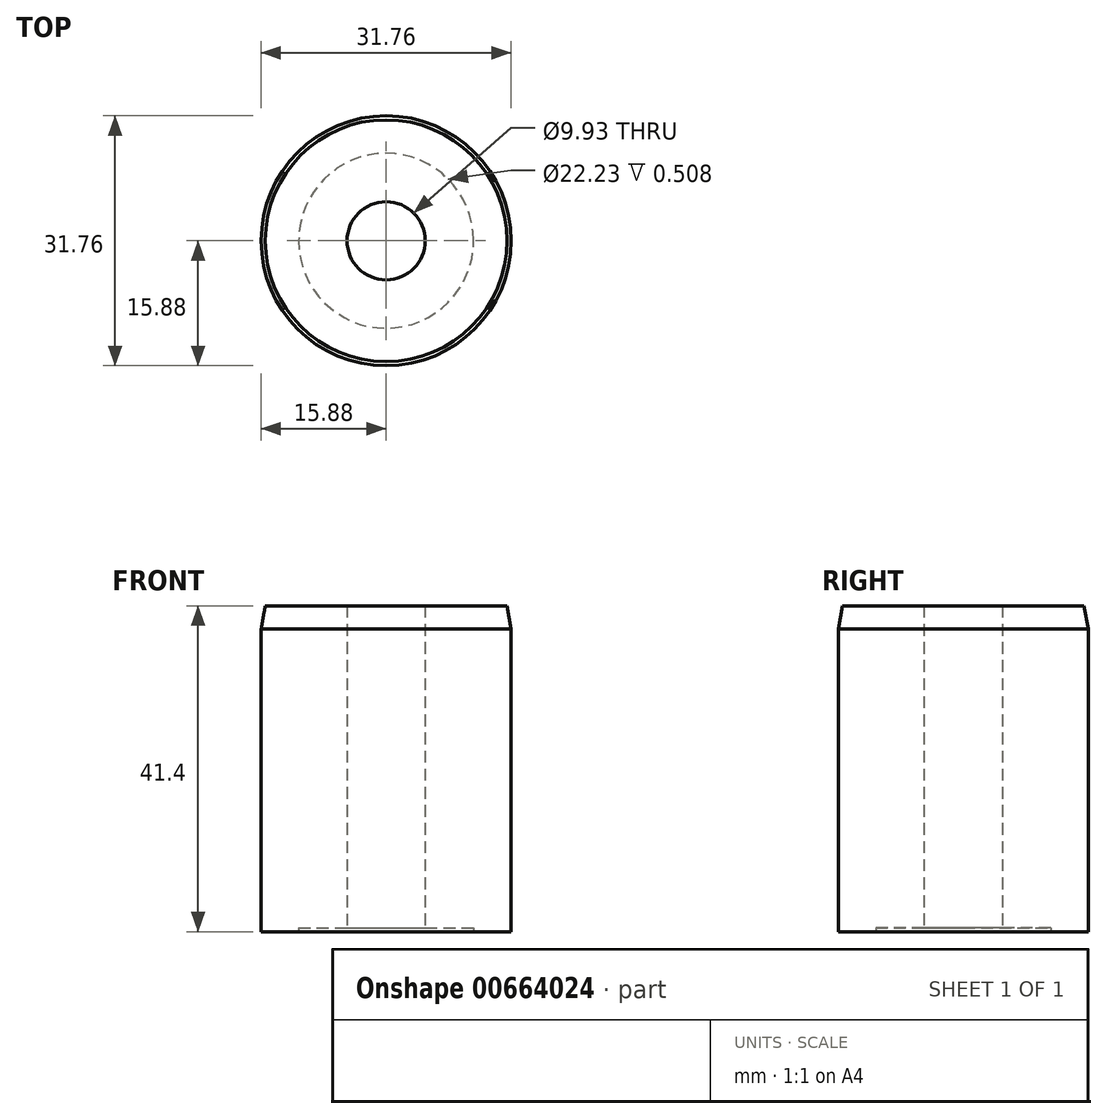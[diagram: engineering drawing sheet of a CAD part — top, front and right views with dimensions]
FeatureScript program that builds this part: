
annotation { "Feature Type Name" : "Feature", "Feature Type Description" : "" }
export const myFeature = defineFeature(function(context is Context, id is Id, definition is map)
    precondition{}
    {
        {
            var Q0;
            Q0=qCreatedBy(makeId("Front.planeOp"),FACE);
            var sketch = newSketch(context, id + "F0", { "sketchPlane" : qUnion([Q0])});
            skLineSegment(sketch, "E0", {"start": v(0, 0) * mm, "end": v(0, 64.44) * mm, "construction": true});
            skLineSegment(sketch, "E1", {"start": v(4.97, 0.5) * mm, "end": v(11.11, 0.5) * mm});
            skLineSegment(sketch, "E2", {"start": v(11.11, 0.5) * mm, "end": v(11.11, 0) * mm});
            skLineSegment(sketch, "E3", {"start": v(11.11, 0) * mm, "end": v(15.88, 0) * mm});
            skLineSegment(sketch, "E4", {"start": v(15.88, 0) * mm, "end": v(15.88, 38.48) * mm});
            skLineSegment(sketch, "E5", {"start": v(15.88, 38.48) * mm, "end": v(15.36, 41.4) * mm});
            skLineSegment(sketch, "E6", {"start": v(15.36, 41.4) * mm, "end": v(4.97, 41.4) * mm});
            skLineSegment(sketch, "E7", {"start": v(4.97, 41.4) * mm, "end": v(4.97, 0.5) * mm});
            skSolve(sketch);
        }
        {
            var Q0;
            Q0=makeQuery(id+"F0.imprint","IMPRINT",FACE,{"disambiguationData":[TD([[makeQuery(id+"F0.imprint","IMPRINT",EDGE,{"derivedFrom":sQuery(id+"F0.wireOp",EDGE,"E1")}),1.0]])]});
            var Q1;
            Q1=sQuery(id+"F0.wireOp",EDGE,"E0");
            revolve(context, id + "F1", {"entities" : qUnion([Q0]), "axis" : qUnion([Q1]), "revolveType" : RevolveType.FULL});
        }
    });
